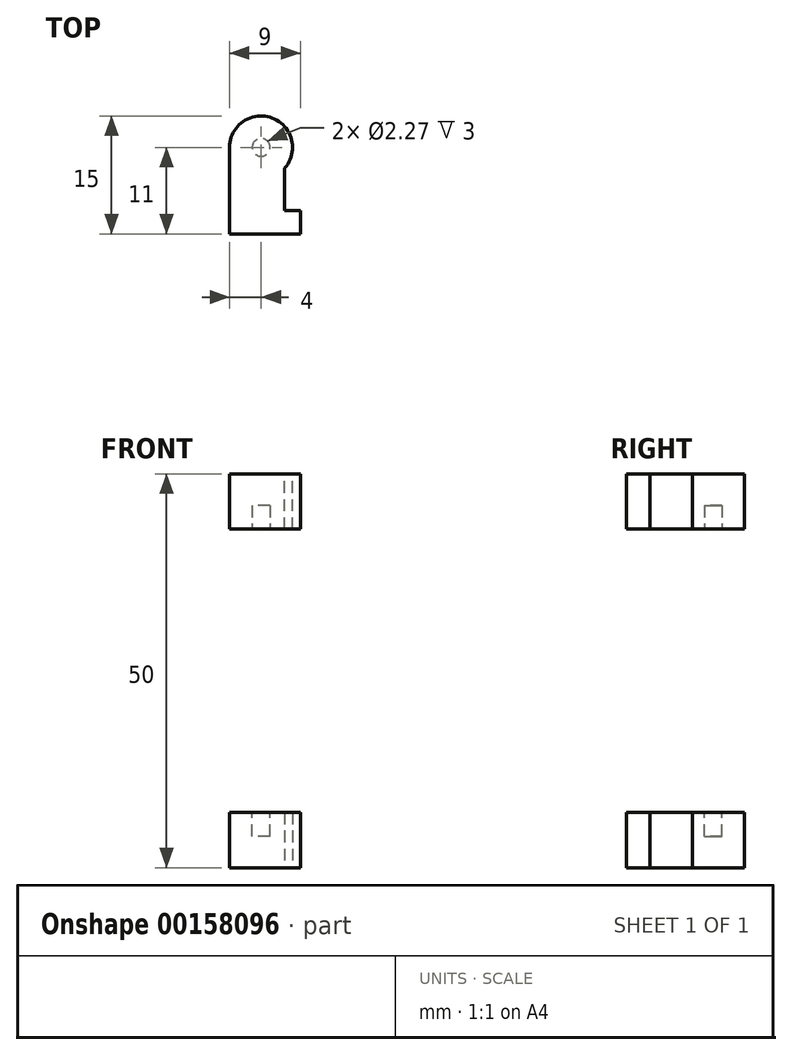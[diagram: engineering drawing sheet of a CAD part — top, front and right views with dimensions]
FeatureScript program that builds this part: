
annotation { "Feature Type Name" : "Feature", "Feature Type Description" : "" }
export const myFeature = defineFeature(function(context is Context, id is Id, definition is map)
    precondition{}
    {
        {
            var Q0;
            Q0=qCreatedBy(makeId("Top.planeOp"),FACE);
            var sketch = newSketch(context, id + "F0", { "sketchPlane" : qUnion([Q0])});
            skCircle(sketch, "E0", {"center": v(0, 8) * mm, "radius": 4 * mm});
            skLineSegment(sketch, "E1", {"start": v(5, 0) * mm, "end": v(5, -3) * mm});
            skLineSegment(sketch, "E2", {"start": v(5, -3) * mm, "end": v(-4, -3) * mm});
            skLineSegment(sketch, "E3", {"start": v(-4, -3) * mm, "end": v(-4, 8) * mm});
            skLineSegment(sketch, "E4", {"start": v(5, 0) * mm, "end": v(3, 0) * mm});
            skLineSegment(sketch, "E5", {"start": v(3, 0) * mm, "end": v(3, 5.35) * mm});
            skSolve(sketch);
        }
        {
            var Q0;
            Q0=makeQuery(id+"F0.imprint","IMPRINT",FACE,{"disambiguationData":[TD([[makeQuery(id+"F0.imprint","IMPRINT",EDGE,{"derivedFrom":sQuery(id+"F0.wireOp",EDGE,"E1")}),-1.0]])]});
            var Q1;
            {var subQ0=sQuery(id+"F0.wireOp",EDGE,"E0");var subQ1=makeQuery(id+"F0.imprint","INTERSECT",VERTEX,{"derivedFrom":[subQ0,sQuery(id+"F0.wireOp",EDGE,"E3")]});Q1=makeQuery(id+"F0.imprint","IMPRINT",FACE,{"disambiguationData":[TD([[makeQuery(id+"F0.imprint","IMPRINT",EDGE,{"disambiguationData":[TD([[subQ1,-1.0]])],"derivedFrom":subQ0}),1.0]])]});}
            extrude(context, id + "F1", {"entities" : qUnion([Q0, Q1]), "depth" : 7 * mm});
        }
        {
            var Q0;
            Q0=makeQuery(id+"F1.opExtrude","CAP_FACE",FACE,{"disambiguationData":[OSD([sQuery(id+"F0.wireOp",EDGE,"E0"),sQuery(id+"F0.wireOp",EDGE,"E1"),sQuery(id+"F0.wireOp",EDGE,"E2"),sQuery(id+"F0.wireOp",EDGE,"E3"),sQuery(id+"F0.wireOp",EDGE,"E4"),sQuery(id+"F0.wireOp",EDGE,"E5")])],"isStart":false});
            var sketch = newSketch(context, id + "F2", { "sketchPlane" : qUnion([Q0])});
            skCircle(sketch, "E6", {"center": v(0, 8) * mm, "radius": 1.13 * mm});
            skSolve(sketch);
        }
        {
            var Q0;
            Q0=qCreatedBy(makeId("Top.planeOp"),FACE);
            cPlane(context, id + "F3", {"entities" : qUnion([Q0]), "cplaneType" : CPlaneType.OFFSET, "offset" : 25 * mm, "width" : 150 * mm, "height" : 150 * mm});
        }
        {
            var Q0;
            Q0=makeQuery(id+"F2.imprint","IMPRINT",FACE,{"disambiguationData":[TD([[makeQuery(id+"F2.imprint","IMPRINT",EDGE,{"derivedFrom":sQuery(id+"F2.wireOp",EDGE,"E6")}),1.0]])]});
            extrude(context, id + "F4", {"entities" : qUnion([Q0]), "operationType" : NewBodyOperationType.REMOVE, "oppositeDirection" : true, "depth" : 3 * mm});
        }
        {
            var Q0;
            Q0=makeQuery(id+"F1.opExtrude","SWEPT_BODY",BODY,{"disambiguationData":[OSD([sQuery(id+"F0.wireOp",EDGE,"E0"),sQuery(id+"F0.wireOp",EDGE,"E1"),sQuery(id+"F0.wireOp",EDGE,"E2"),sQuery(id+"F0.wireOp",EDGE,"E3"),sQuery(id+"F0.wireOp",EDGE,"E4"),sQuery(id+"F0.wireOp",EDGE,"E5")])]});
            var Q1;
            Q1=qCreatedBy(id+"F3.planeOp",FACE);
            mirror(context, id + "F5", {"entities" : qUnion([Q0]), "mirrorPlane" : qUnion([Q1])});
        }
    });
